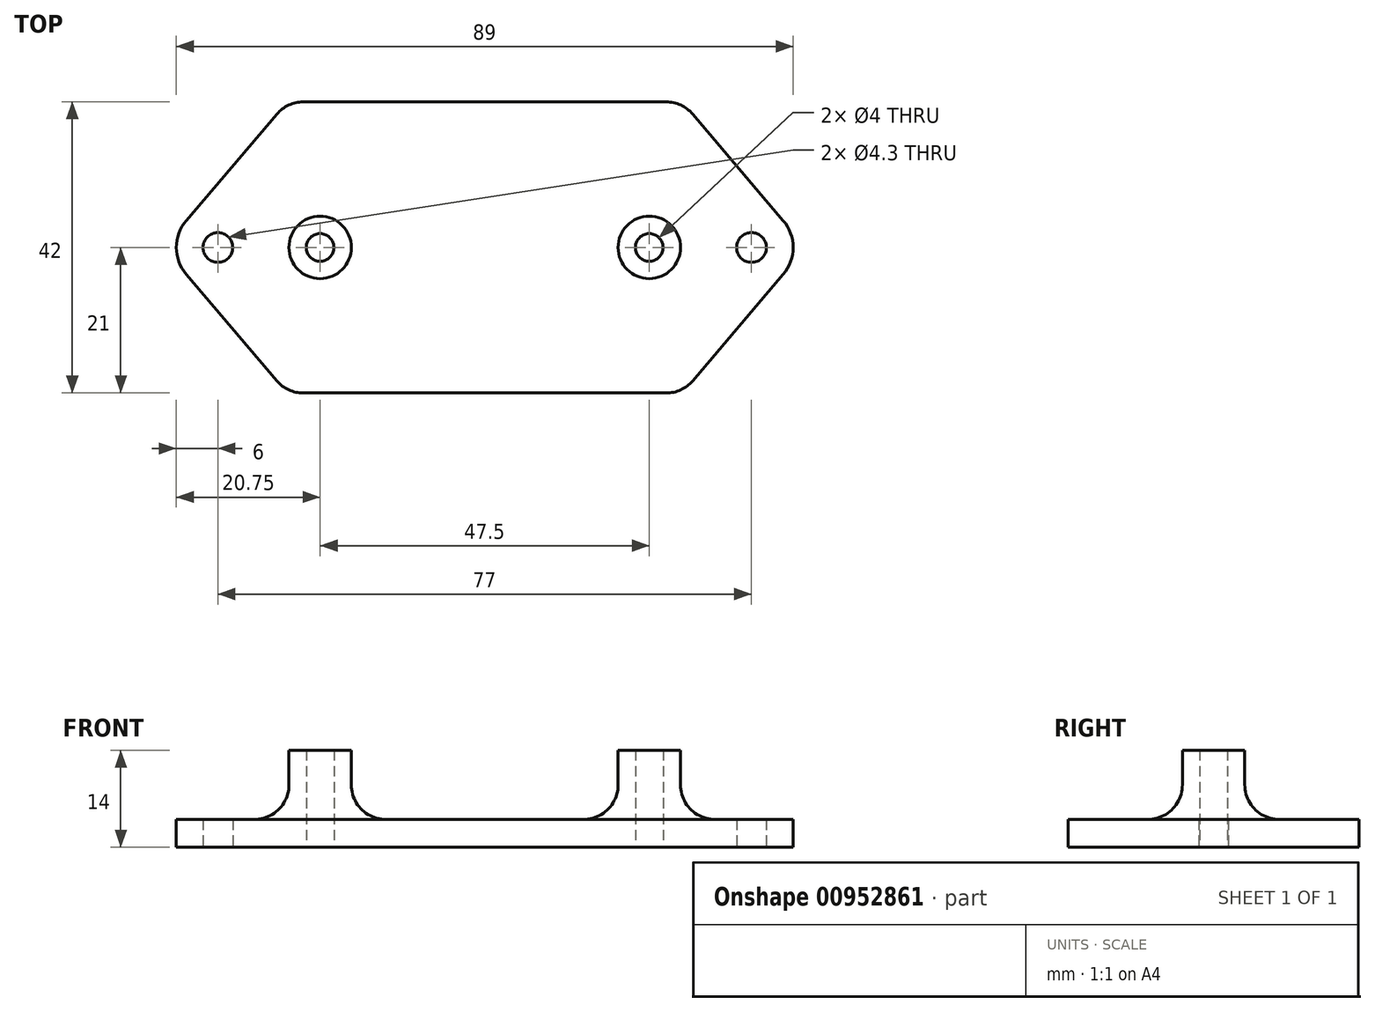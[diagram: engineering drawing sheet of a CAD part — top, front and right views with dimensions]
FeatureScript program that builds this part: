
annotation { "Feature Type Name" : "Feature", "Feature Type Description" : "" }
export const myFeature = defineFeature(function(context is Context, id is Id, definition is map)
    precondition{}
    {
        {
            var Q0;
            Q0=qCreatedBy(makeId("Top.planeOp"),FACE);
            var sketch = newSketch(context, id + "F0", { "sketchPlane" : qUnion([Q0])});
            skLineSegment(sketch, "E0.bottom", {"start": v(-28.5, -21) * mm, "end": v(28.5, -21) * mm});
            skLineSegment(sketch, "E0.top", {"start": v(-28.5, 21) * mm, "end": v(28.5, 21) * mm});
            skLineSegment(sketch, "E0.left", {"start": v(-28.5, -21) * mm, "end": v(-28.5, 21) * mm});
            skLineSegment(sketch, "E0.right", {"start": v(28.5, -21) * mm, "end": v(28.5, 21) * mm});
            skPoint(sketch, "E0.middle", {"position": v(0, 0) * mm});
            skCircle(sketch, "E1", {"center": v(-23.75, 0) * mm, "radius": 2 * mm});
            skCircle(sketch, "E2", {"center": v(23.75, 0) * mm, "radius": 2 * mm});
            skLineSegment(sketch, "E3", {"start": v(-23.75, 0) * mm, "end": v(23.75, 0) * mm, "construction": true});
            skCircle(sketch, "E4", {"center": v(-23.75, 0) * mm, "radius": 4.5 * mm});
            skCircle(sketch, "E5", {"center": v(23.75, 0) * mm, "radius": 4.5 * mm});
            skCircle(sketch, "E6", {"center": v(-38.5, 0) * mm, "radius": 6 * mm});
            skLineSegment(sketch, "E7", {"start": v(-28.5, 21) * mm, "end": v(-43.07, 3.89) * mm});
            skLineSegment(sketch, "E8", {"start": v(-28.5, -21) * mm, "end": v(-43.07, -3.89) * mm});
            skCircle(sketch, "E9", {"center": v(-38.5, 0) * mm, "radius": 2.15 * mm});
            skLineSegment(sketch, "E10.MirrorCS", {"start": v(28.5, 21) * mm, "end": v(43.07, 3.89) * mm});
            skCircle(sketch, "E11.MirrorC", {"center": v(38.5, 0) * mm, "radius": 6 * mm});
            skCircle(sketch, "E12.MirrorC", {"center": v(38.5, 0) * mm, "radius": 2.15 * mm});
            skLineSegment(sketch, "E13.MirrorCS", {"start": v(28.5, -21) * mm, "end": v(43.07, -3.89) * mm});
            skSolve(sketch);
        }
        {
            var Q0;
            Q0 = qSketchRegion(id + "F0", true);
            var Q1;
            Q1=makeQuery(id+"F0.imprint","IMPRINT",FACE,{"disambiguationData":[TD([[makeQuery(id+"F0.imprint","IMPRINT",EDGE,{"derivedFrom":sQuery(id+"F0.wireOp",EDGE,"E1")}),-1.0]])]});
            var Q2;
            Q2=makeQuery(id+"F0.imprint","IMPRINT",FACE,{"disambiguationData":[TD([[makeQuery(id+"F0.imprint","IMPRINT",EDGE,{"derivedFrom":sQuery(id+"F0.wireOp",EDGE,"E2")}),-1.0]])]});
            extrude(context, id + "F1", {"entities" : qUnion([Q0, Q1, Q2]), "depth" : 4 * mm, "offsetDistance" : 25 * mm});
        }
        {
            var Q0;
            Q0=makeQuery(id+"F0.imprint","IMPRINT",FACE,{"disambiguationData":[TD([[makeQuery(id+"F0.imprint","IMPRINT",EDGE,{"derivedFrom":sQuery(id+"F0.wireOp",EDGE,"E1")}),-1.0]])]});
            var Q1;
            Q1=makeQuery(id+"F0.imprint","IMPRINT",FACE,{"disambiguationData":[TD([[makeQuery(id+"F0.imprint","IMPRINT",EDGE,{"derivedFrom":sQuery(id+"F0.wireOp",EDGE,"E2")}),-1.0]])]});
            extrude(context, id + "F2", {"entities" : qUnion([Q0, Q1]), "operationType" : NewBodyOperationType.ADD, "depth" : 14 * mm, "offsetDistance" : 25 * mm});
        }
        {
            var Q0;
            Q0=makeQuery(id+"F1.opExtrude","SWEPT_EDGE",EDGE,{"disambiguationData":[OSD([sQuery(id+"F0.wireOp",EDGE,"E0.top"),sQuery(id+"F0.wireOp",EDGE,"E0.left"),sQuery(id+"F0.wireOp",EDGE,"E7")])]});
            var Q1;
            Q1=makeQuery(id+"F1.opExtrude","SWEPT_EDGE",EDGE,{"disambiguationData":[OSD([sQuery(id+"F0.wireOp",EDGE,"E0.bottom"),sQuery(id+"F0.wireOp",EDGE,"E0.left"),sQuery(id+"F0.wireOp",EDGE,"E8")])]});
            var Q2;
            Q2=makeQuery(id+"F1.opExtrude","SWEPT_EDGE",EDGE,{"disambiguationData":[OSD([sQuery(id+"F0.wireOp",EDGE,"E0.bottom"),sQuery(id+"F0.wireOp",EDGE,"E0.right"),sQuery(id+"F0.wireOp",EDGE,"E13.MirrorCS")])]});
            var Q3;
            Q3=makeQuery(id+"F1.opExtrude","SWEPT_EDGE",EDGE,{"disambiguationData":[OSD([sQuery(id+"F0.wireOp",EDGE,"E0.top"),sQuery(id+"F0.wireOp",EDGE,"E0.right"),sQuery(id+"F0.wireOp",EDGE,"E10.MirrorCS")])]});
            var Q4;
            Q4=makeQuery(id+"F2.boolean.opBoolean","INTERSECT",EDGE,{"derivedFrom":[makeQuery(id+"F1.opExtrude","CAP_FACE",FACE,{"disambiguationData":[OSD([sQuery(id+"F0.wireOp",EDGE,"E0.bottom"),sQuery(id+"F0.wireOp",EDGE,"E0.top"),sQuery(id+"F0.wireOp",EDGE,"E1"),sQuery(id+"F0.wireOp",EDGE,"E2"),sQuery(id+"F0.wireOp",EDGE,"E6"),sQuery(id+"F0.wireOp",EDGE,"E7"),sQuery(id+"F0.wireOp",EDGE,"E8"),sQuery(id+"F0.wireOp",EDGE,"E9"),sQuery(id+"F0.wireOp",EDGE,"E10.MirrorCS"),sQuery(id+"F0.wireOp",EDGE,"E11.MirrorC"),sQuery(id+"F0.wireOp",EDGE,"E12.MirrorC"),sQuery(id+"F0.wireOp",EDGE,"E13.MirrorCS")])],"isStart":false}),makeQuery(id+"F2.opExtrude","SWEPT_FACE",FACE,{"disambiguationData":[OSD([sQuery(id+"F0.wireOp",EDGE,"E4")])]})]});
            var Q5;
            Q5=makeQuery(id+"F2.boolean.opBoolean","INTERSECT",EDGE,{"derivedFrom":[makeQuery(id+"F1.opExtrude","CAP_FACE",FACE,{"disambiguationData":[OSD([sQuery(id+"F0.wireOp",EDGE,"E0.bottom"),sQuery(id+"F0.wireOp",EDGE,"E0.top"),sQuery(id+"F0.wireOp",EDGE,"E1"),sQuery(id+"F0.wireOp",EDGE,"E2"),sQuery(id+"F0.wireOp",EDGE,"E6"),sQuery(id+"F0.wireOp",EDGE,"E7"),sQuery(id+"F0.wireOp",EDGE,"E8"),sQuery(id+"F0.wireOp",EDGE,"E9"),sQuery(id+"F0.wireOp",EDGE,"E10.MirrorCS"),sQuery(id+"F0.wireOp",EDGE,"E11.MirrorC"),sQuery(id+"F0.wireOp",EDGE,"E12.MirrorC"),sQuery(id+"F0.wireOp",EDGE,"E13.MirrorCS")])],"isStart":false}),makeQuery(id+"F2.opExtrude","SWEPT_FACE",FACE,{"disambiguationData":[OSD([sQuery(id+"F0.wireOp",EDGE,"E5")])]})]});
            fillet(context, id + "F3", {"entities" : qUnion([Q0, Q1, Q2, Q3, Q4, Q5]), "radius" : 5 * mm, "tangentPropagation" : true, "allowEdgeOverflow" : false});
        }
    });
